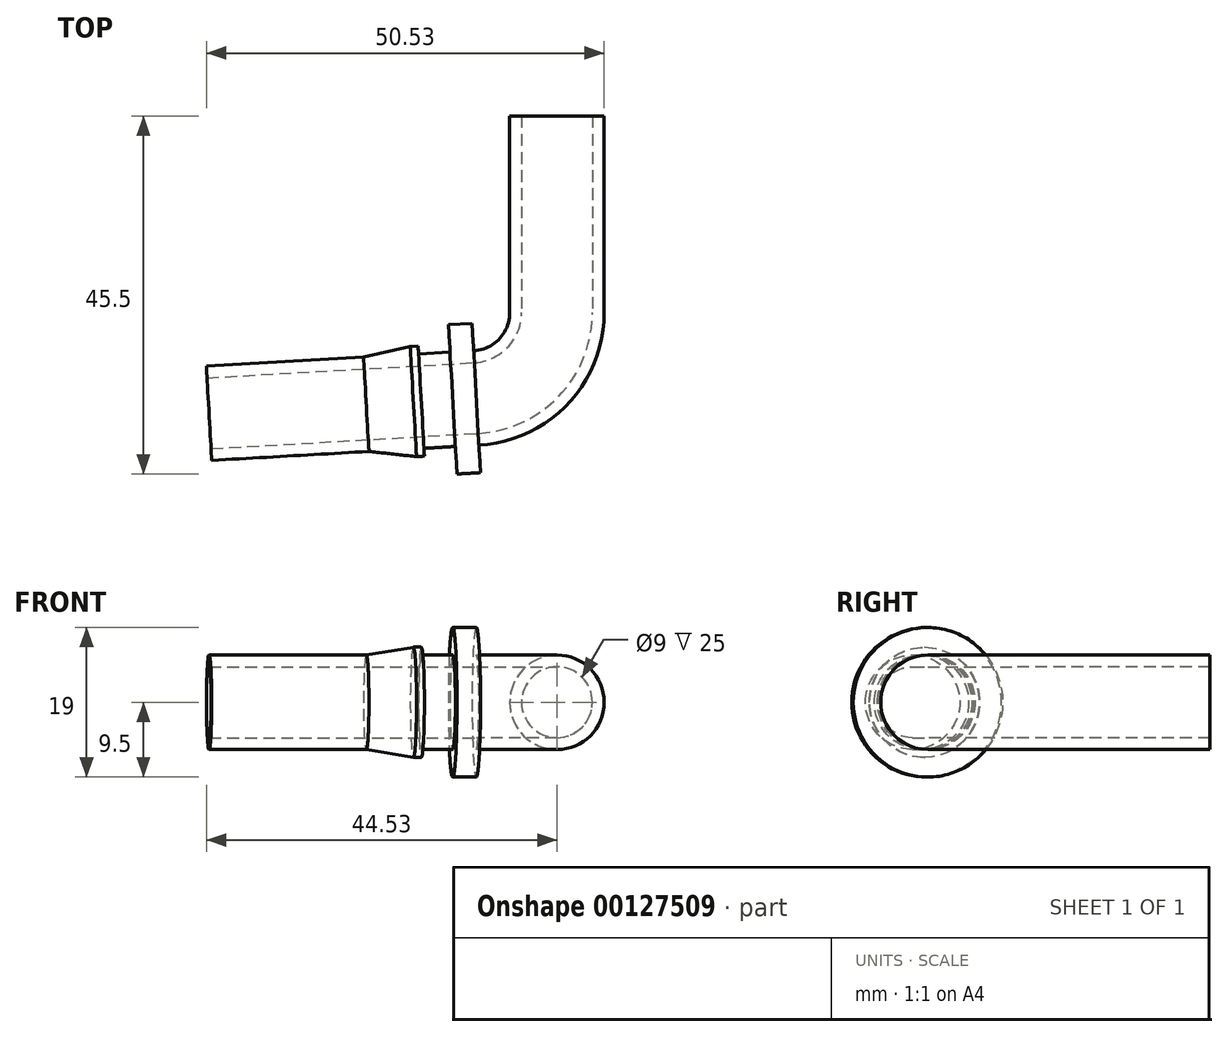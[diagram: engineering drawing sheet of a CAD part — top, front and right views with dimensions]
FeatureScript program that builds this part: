
annotation { "Feature Type Name" : "Feature", "Feature Type Description" : "" }
export const myFeature = defineFeature(function(context is Context, id is Id, definition is map)
    precondition{}
    {
        {
            var Q0;
            Q0=qCreatedBy(makeId("Top.planeOp"),FACE);
            var sketch = newSketch(context, id + "F0", { "sketchPlane" : qUnion([Q0])});
            skArc(sketch, "E0", {"start": v(0, -5) * mm, "mid": v(3.35, -3.43) * mm, "end": v(4.72, 0) * mm});
            skLineSegment(sketch, "E1", {"start": v(0, 0) * mm, "end": v(0, -5) * mm});
            skLineSegment(sketch, "E2", {"start": v(0, 0) * mm, "end": v(4.72, 0) * mm});
            skSolve(sketch);
        }
        {
            var Q0;
            Q0=qCreatedBy(makeId("Front.planeOp"),FACE);
            var sketch = newSketch(context, id + "F1", { "sketchPlane" : qUnion([Q0])});
            skCircle(sketch, "E3", {"center": v(10.58, 0) * mm, "radius": 4.5 * mm});
            skCircle(sketch, "E4", {"center": v(10.58, 0) * mm, "radius": 6 * mm});
            skSolve(sketch);
        }
        {
            var Q0;
            Q0=makeQuery(id+"F1.imprint","IMPRINT",FACE,{"disambiguationData":[TD([[makeQuery(id+"F1.imprint","IMPRINT",EDGE,{"derivedFrom":sQuery(id+"F1.wireOp",EDGE,"E3")}),-1.0]])]});
            extrude(context, id + "F2", {"entities" : qUnion([Q0]), "oppositeDirection" : true, "depth" : 25 * mm});
        }
        {
            var Q0;
            Q0=makeQuery(id+"F2.opExtrude","CAP_FACE",FACE,{"disambiguationData":[OSD([sQuery(id+"F1.wireOp",EDGE,"E3"),sQuery(id+"F1.wireOp",EDGE,"E4")])],"isStart":true});
            var Q1;
            Q1=sQuery(id+"F0.wireOp",EDGE,"E0");
            sweep(context, id + "F3", {"operationType" : NewBodyOperationType.ADD, "profiles" : qUnion([Q0]), "path" : qUnion([Q1])});
        }
        {
            var Q0;
            Q0=makeQuery(id+"F3.opSweep","CAP_FACE",FACE,{"disambiguationData":[OSD([sQuery(id+"F0.wireOp",VERTEX,"E0.start"),sQuery(id+"F1.wireOp",EDGE,"E3"),sQuery(id+"F1.wireOp",EDGE,"E4")])],"isStart":false});
            var sketch = newSketch(context, id + "F4", { "sketchPlane" : qUnion([Q0])});
            skCircle(sketch, "E5", {"center": v(10.85, 0) * mm, "radius": 9.5 * mm});
            skSolve(sketch);
        }
        {
            var Q0;
            Q0=makeQuery(id+"F4.imprint","IMPRINT",FACE,{"disambiguationData":[TD([[makeQuery(id+"F4.imprint","IMPRINT",EDGE,{"derivedFrom":sQuery(id+"F4.wireOp",EDGE,"E5")}),1.0]])]});
            var Q1;
            {var subQ0=sQuery(id+"F0.wireOp",VERTEX,"E0.start");Q1=makeQuery(id+"F4.imprint","IMPRINT",FACE,{"disambiguationData":[TD([[makeQuery(id+"F4.imprint","IMPRINT",EDGE,{"derivedFrom":makeQuery(id+"F3.opSweep","CAP_EDGE",EDGE,{"disambiguationData":[OSD([subQ0,sQuery(id+"F1.wireOp",EDGE,"E3")])],"isStart":false})}),-1.0]])]});}
            extrude(context, id + "F5", {"entities" : qUnion([Q0, Q1]), "operationType" : NewBodyOperationType.ADD, "depth" : 3 * mm});
        }
        {
            var Q0;
            Q0=makeQuery(id+"F5.opExtrude","CAP_FACE",FACE,{"disambiguationData":[OSD([sQuery(id+"F0.wireOp",VERTEX,"E0.start"),sQuery(id+"F1.wireOp",EDGE,"E3"),sQuery(id+"F4.wireOp",EDGE,"E5")])],"isStart":false});
            var sketch = newSketch(context, id + "F6", { "sketchPlane" : qUnion([Q0])});
            skCircle(sketch, "E6", {"center": v(10.85, 0) * mm, "radius": 6 * mm});
            skSolve(sketch);
        }
        {
            var Q0;
            Q0=makeQuery(id+"F6.imprint","IMPRINT",FACE,{"disambiguationData":[TD([[makeQuery(id+"F6.imprint","IMPRINT",EDGE,{"derivedFrom":sQuery(id+"F6.wireOp",EDGE,"E6")}),1.0]])]});
            extrude(context, id + "F7", {"entities" : qUnion([Q0]), "operationType" : NewBodyOperationType.ADD, "depth" : 4 * mm});
        }
        {
            var Q0;
            Q0=makeQuery(id+"F7.opExtrude","CAP_FACE",FACE,{"disambiguationData":[OSD([sQuery(id+"F0.wireOp",VERTEX,"E0.start"),sQuery(id+"F1.wireOp",EDGE,"E3"),sQuery(id+"F6.wireOp",EDGE,"E6")])],"isStart":false});
            var sketch = newSketch(context, id + "F8", { "sketchPlane" : qUnion([Q0])});
            skCircle(sketch, "E7", {"center": v(10.85, 0) * mm, "radius": 7 * mm});
            skSolve(sketch);
        }
        {
            var Q0;
            Q0=makeQuery(id+"F8.imprint","IMPRINT",FACE,{"disambiguationData":[TD([[makeQuery(id+"F8.imprint","IMPRINT",EDGE,{"derivedFrom":makeQuery(id+"F7.opExtrude","CAP_EDGE",EDGE,{"disambiguationData":[OSD([sQuery(id+"F6.wireOp",EDGE,"E6")])],"isStart":false})}),1.0]])]});
            var Q1;
            Q1=makeQuery(id+"F8.imprint","IMPRINT",FACE,{"disambiguationData":[TD([[makeQuery(id+"F8.imprint","IMPRINT",EDGE,{"derivedFrom":sQuery(id+"F8.wireOp",EDGE,"E7")}),1.0]])]});
            extrude(context, id + "F9", {"entities" : qUnion([Q0, Q1]), "operationType" : NewBodyOperationType.ADD, "depth" : 7 * mm});
        }
        {
            var Q0;
            Q0=makeQuery(id+"F9.opExtrude","CAP_EDGE",EDGE,{"disambiguationData":[OSD([sQuery(id+"F8.wireOp",EDGE,"E7")])],"isStart":false});
            chamfer(context, id + "F10", {"entities" : qUnion([Q0]), "chamferType" : ChamferType.TWO_OFFSETS, "width1" : 1 * mm, "oppositeDirection" : false, "width2" : 6 * mm, "tangentPropagation" : true});
        }
        {
            var Q0;
            Q0=makeQuery(id+"F9.opExtrude","CAP_FACE",FACE,{"disambiguationData":[OSD([sQuery(id+"F0.wireOp",VERTEX,"E0.start"),sQuery(id+"F1.wireOp",EDGE,"E3"),sQuery(id+"F8.wireOp",EDGE,"E7")])],"isStart":false});
            var sketch = newSketch(context, id + "F11", { "sketchPlane" : qUnion([Q0])});
            skSolve(sketch);
        }
        {
            var Q0;
            Q0 = qSketchRegion(id + "F11", true);
            var Q1;
            {var subQ0=sQuery(id+"F1.wireOp",EDGE,"E3");var subQ1=sQuery(id+"F0.wireOp",VERTEX,"E0.start");Q1=makeQuery(id+"F11.imprint","IMPRINT",FACE,{"disambiguationData":[TD([[makeQuery(id+"F11.imprint","IMPRINT",EDGE,{"derivedFrom":makeQuery(id+"F9.opExtrude","CAP_EDGE",EDGE,{"disambiguationData":[OSD([subQ1,subQ0])],"isStart":false})}),-1.0]])]});}
            extrude(context, id + "F12", {"entities" : qUnion([Q0, Q1]), "operationType" : NewBodyOperationType.ADD, "depth" : 20 * mm});
        }
    });
